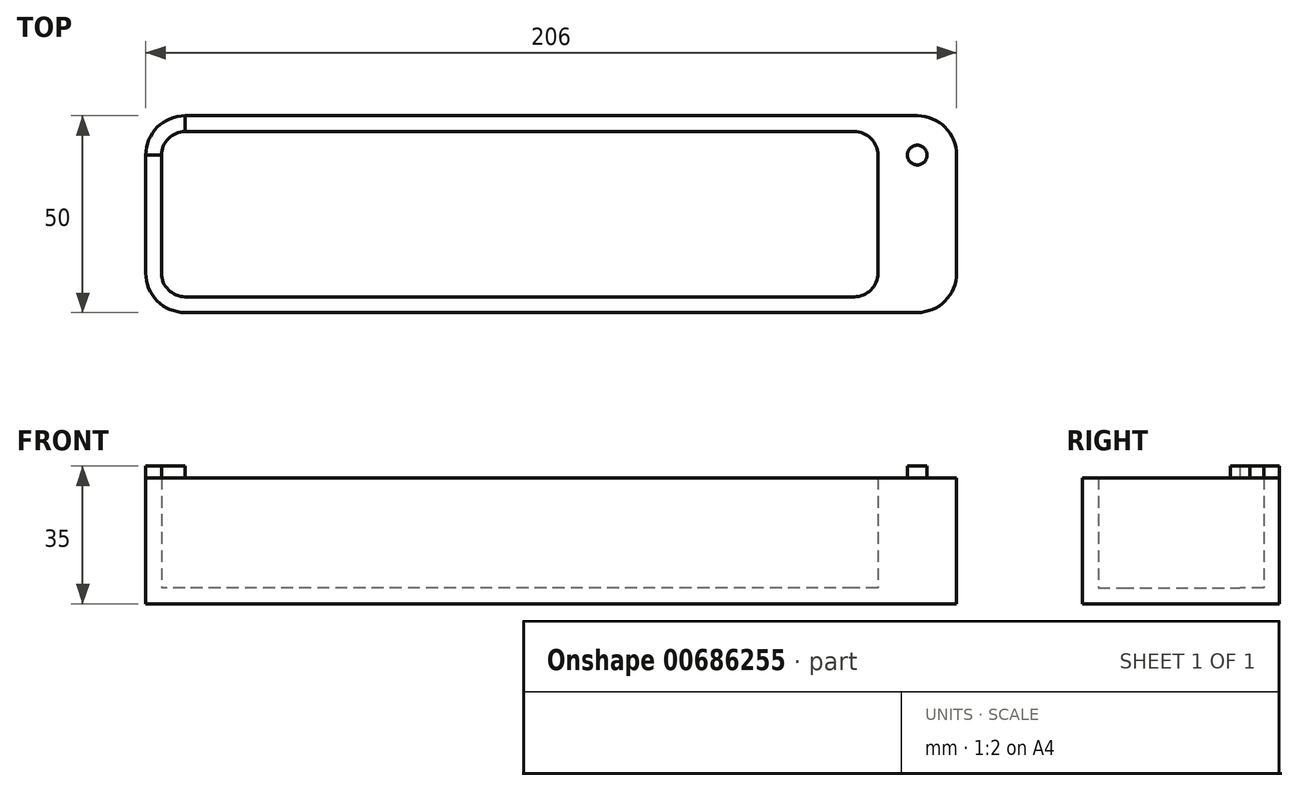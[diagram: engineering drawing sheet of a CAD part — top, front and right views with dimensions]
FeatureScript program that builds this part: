
annotation { "Feature Type Name" : "Feature", "Feature Type Description" : "" }
export const myFeature = defineFeature(function(context is Context, id is Id, definition is map)
    precondition{}
    {
        {
            var Q0;
            Q0=qCreatedBy(makeId("Top.planeOp"),FACE);
            var sketch = newSketch(context, id + "F0", { "sketchPlane" : qUnion([Q0])});
            skLineSegment(sketch, "E0.bottom", {"start": v(85, -21) * mm, "end": v(-85, -21) * mm});
            skLineSegment(sketch, "E0.top", {"start": v(85, 21) * mm, "end": v(-85, 21) * mm});
            skLineSegment(sketch, "E0.left", {"start": v(91, -15) * mm, "end": v(91, 15) * mm});
            skLineSegment(sketch, "E0.right", {"start": v(-91, -15) * mm, "end": v(-91, 15) * mm});
            skPoint(sketch, "E0.middle", {"position": v(0, 0) * mm});
            skPoint(sketch, "E1.visualSharp", {"position": v(91, -21) * mm});
            skArc(sketch, "E1.filletArc", {"start": v(85, -21) * mm, "mid": v(89.24, -19.24) * mm, "end": v(91, -15) * mm});
            skPoint(sketch, "E2.visualSharp", {"position": v(91, 21) * mm});
            skArc(sketch, "E2.filletArc", {"start": v(91, 15) * mm, "mid": v(89.24, 19.24) * mm, "end": v(85, 21) * mm});
            skPoint(sketch, "E3.visualSharp", {"position": v(-91, 21) * mm});
            skArc(sketch, "E3.filletArc", {"start": v(-85, 21) * mm, "mid": v(-89.24, 19.24) * mm, "end": v(-91, 15) * mm});
            skPoint(sketch, "E4.visualSharp", {"position": v(-91, -21) * mm});
            skArc(sketch, "E4.filletArc", {"start": v(-91, -15) * mm, "mid": v(-89.24, -19.24) * mm, "end": v(-85, -21) * mm});
            skLineSegment(sketch, "E5.bottom", {"start": v(101, -25) * mm, "end": v(-85, -25) * mm});
            skLineSegment(sketch, "E5.top", {"start": v(101, 25) * mm, "end": v(-85, 25) * mm});
            skLineSegment(sketch, "E5.left", {"start": v(111, -15) * mm, "end": v(111, 15) * mm});
            skLineSegment(sketch, "E5.right", {"start": v(-95, -15) * mm, "end": v(-95, 15) * mm});
            skPoint(sketch, "E6.visualSharp", {"position": v(111, -25) * mm});
            skArc(sketch, "E6.filletArc", {"start": v(101, -25) * mm, "mid": v(108.07, -22.07) * mm, "end": v(111, -15) * mm});
            skPoint(sketch, "E7.visualSharp", {"position": v(-95, -25) * mm});
            skArc(sketch, "E7.filletArc", {"start": v(-95, -15) * mm, "mid": v(-92.07, -22.07) * mm, "end": v(-85, -25) * mm});
            skPoint(sketch, "E8.visualSharp", {"position": v(-95, 25) * mm});
            skArc(sketch, "E8.filletArc", {"start": v(-85, 25) * mm, "mid": v(-92.07, 22.07) * mm, "end": v(-95, 15) * mm});
            skPoint(sketch, "E9.visualSharp", {"position": v(111, 25) * mm});
            skArc(sketch, "E9.filletArc", {"start": v(111, 15) * mm, "mid": v(108.07, 22.07) * mm, "end": v(101, 25) * mm});
            skCircle(sketch, "E10", {"center": v(101, 15) * mm, "radius": 2.5 * mm});
            skLineSegment(sketch, "E11", {"start": v(-91, 15) * mm, "end": v(-95, 15) * mm});
            skLineSegment(sketch, "E12", {"start": v(-85, 21) * mm, "end": v(-85, 25) * mm});
            skSolve(sketch);
        }
        {
            var Q0;
            Q0=makeQuery(id+"F0.imprint","IMPRINT",FACE,{"disambiguationData":[TD([[makeQuery(id+"F0.imprint","IMPRINT",EDGE,{"derivedFrom":sQuery(id+"F0.wireOp",EDGE,"E3.filletArc")}),-1.0]])]});
            var Q1;
            Q1=makeQuery(id+"F0.imprint","IMPRINT",FACE,{"disambiguationData":[TD([[makeQuery(id+"F0.imprint","IMPRINT",EDGE,{"derivedFrom":sQuery(id+"F0.wireOp",EDGE,"E0.bottom")}),1.0]])]});
            var Q2;
            Q2=makeQuery(id+"F0.imprint","IMPRINT",FACE,{"disambiguationData":[TD([[makeQuery(id+"F0.imprint","IMPRINT",EDGE,{"derivedFrom":sQuery(id+"F0.wireOp",EDGE,"E10")}),1.0]])]});
            extrude(context, id + "F1", {"entities" : qUnion([Q0, Q1, Q2]), "depth" : 32 * mm, "offsetDistance" : 25 * mm});
        }
        {
            var Q0;
            Q0=makeQuery(id+"F0.imprint","IMPRINT",FACE,{"disambiguationData":[TD([[makeQuery(id+"F0.imprint","IMPRINT",EDGE,{"derivedFrom":sQuery(id+"F0.wireOp",EDGE,"E3.filletArc")}),-1.0]])]});
            var Q1;
            Q1=makeQuery(id+"F0.imprint","IMPRINT",FACE,{"disambiguationData":[TD([[makeQuery(id+"F0.imprint","IMPRINT",EDGE,{"derivedFrom":sQuery(id+"F0.wireOp",EDGE,"E10")}),1.0]])]});
            extrude(context, id + "F2", {"entities" : qUnion([Q0, Q1]), "operationType" : NewBodyOperationType.ADD, "depth" : 35 * mm, "offsetDistance" : 25 * mm});
        }
        {
            var Q0;
            Q0=makeQuery(id+"F0.imprint","IMPRINT",FACE,{"disambiguationData":[TD([[makeQuery(id+"F0.imprint","IMPRINT",EDGE,{"derivedFrom":sQuery(id+"F0.wireOp",EDGE,"E0.bottom")}),-1.0]])]});
            extrude(context, id + "F3", {"entities" : qUnion([Q0]), "operationType" : NewBodyOperationType.ADD, "depth" : 4 * mm, "offsetDistance" : 25 * mm});
        }
        {
            var Q0;
            Q0=makeQuery(id+"F1.opExtrude","CAP_FACE",FACE,{"disambiguationData":[OSD([sQuery(id+"F0.wireOp",EDGE,"E0.bottom"),sQuery(id+"F0.wireOp",EDGE,"E0.top"),sQuery(id+"F0.wireOp",EDGE,"E0.left"),sQuery(id+"F0.wireOp",EDGE,"E0.right"),sQuery(id+"F0.wireOp",EDGE,"E1.filletArc"),sQuery(id+"F0.wireOp",EDGE,"E2.filletArc"),sQuery(id+"F0.wireOp",EDGE,"E3.filletArc"),sQuery(id+"F0.wireOp",EDGE,"E4.filletArc"),sQuery(id+"F0.wireOp",EDGE,"E5.bottom"),sQuery(id+"F0.wireOp",EDGE,"E5.top"),sQuery(id+"F0.wireOp",EDGE,"E5.left"),sQuery(id+"F0.wireOp",EDGE,"E5.right"),sQuery(id+"F0.wireOp",EDGE,"E6.filletArc"),sQuery(id+"F0.wireOp",EDGE,"E7.filletArc"),sQuery(id+"F0.wireOp",EDGE,"E8.filletArc"),sQuery(id+"F0.wireOp",EDGE,"E9.filletArc")])],"isStart":false});
            cPlane(context, id + "F4", {"entities" : qUnion([Q0]), "cplaneType" : CPlaneType.OFFSET, "offset" : 25 * mm, "width" : 150 * mm, "height" : 150 * mm});
        }
    });
